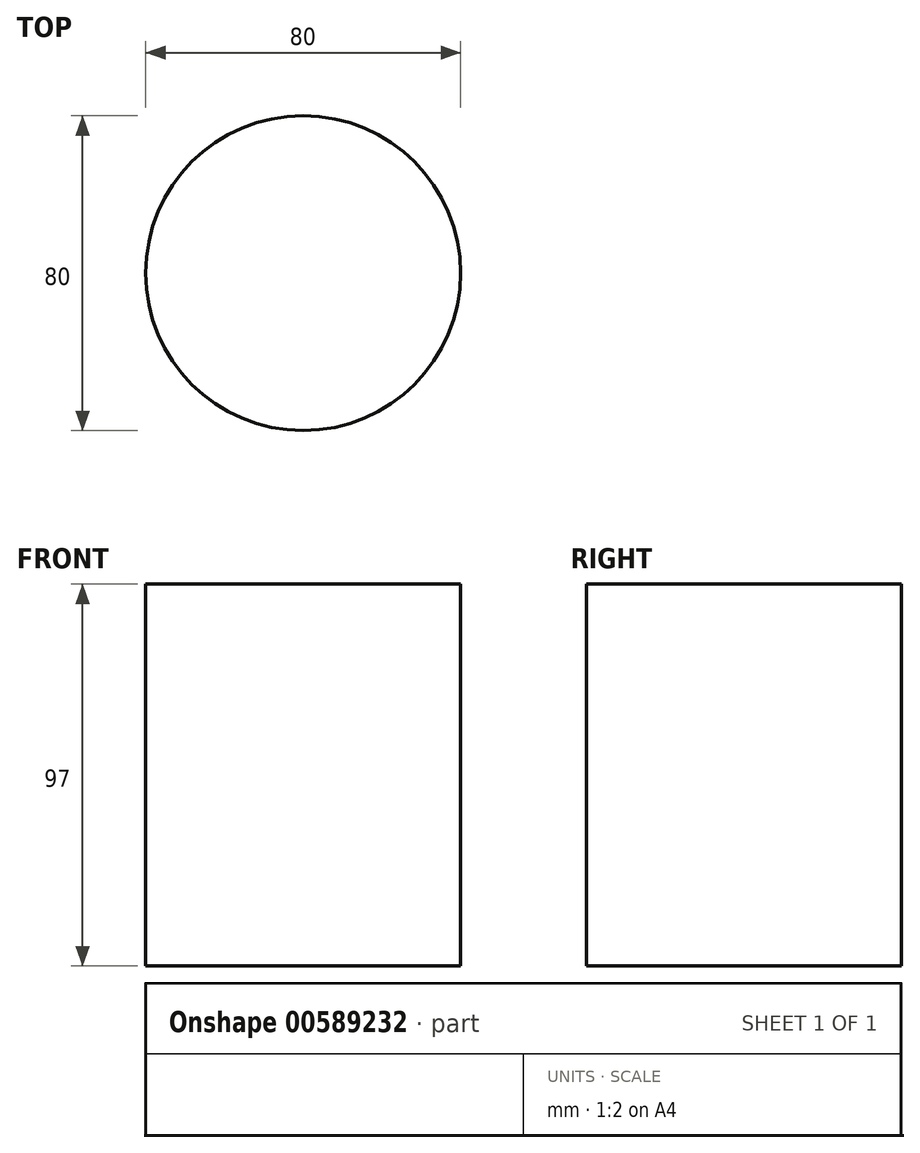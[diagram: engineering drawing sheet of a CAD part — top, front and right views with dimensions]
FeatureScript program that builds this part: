
annotation { "Feature Type Name" : "Feature", "Feature Type Description" : "" }
export const myFeature = defineFeature(function(context is Context, id is Id, definition is map)
    precondition{}
    {
        {
            var Q0;
            Q0=qCreatedBy(makeId("Top.planeOp"),FACE);
            var sketch = newSketch(context, id + "F0", { "sketchPlane" : qUnion([Q0])});
            skCircle(sketch, "E0", {"center": v(0, 0) * mm, "radius": 40 * mm});
            skSolve(sketch);
        }
        {
            var Q0;
            Q0=makeQuery(id+"F0.imprint","IMPRINT",FACE,{"disambiguationData":[TD([[makeQuery(id+"F0.imprint","IMPRINT",EDGE,{"derivedFrom":sQuery(id+"F0.wireOp",EDGE,"E0")}),1.0]])]});
            extrude(context, id + "F1", {"entities" : qUnion([Q0]), "depth" : 97 * mm, "offsetDistance" : 25 * mm});
        }
    });
